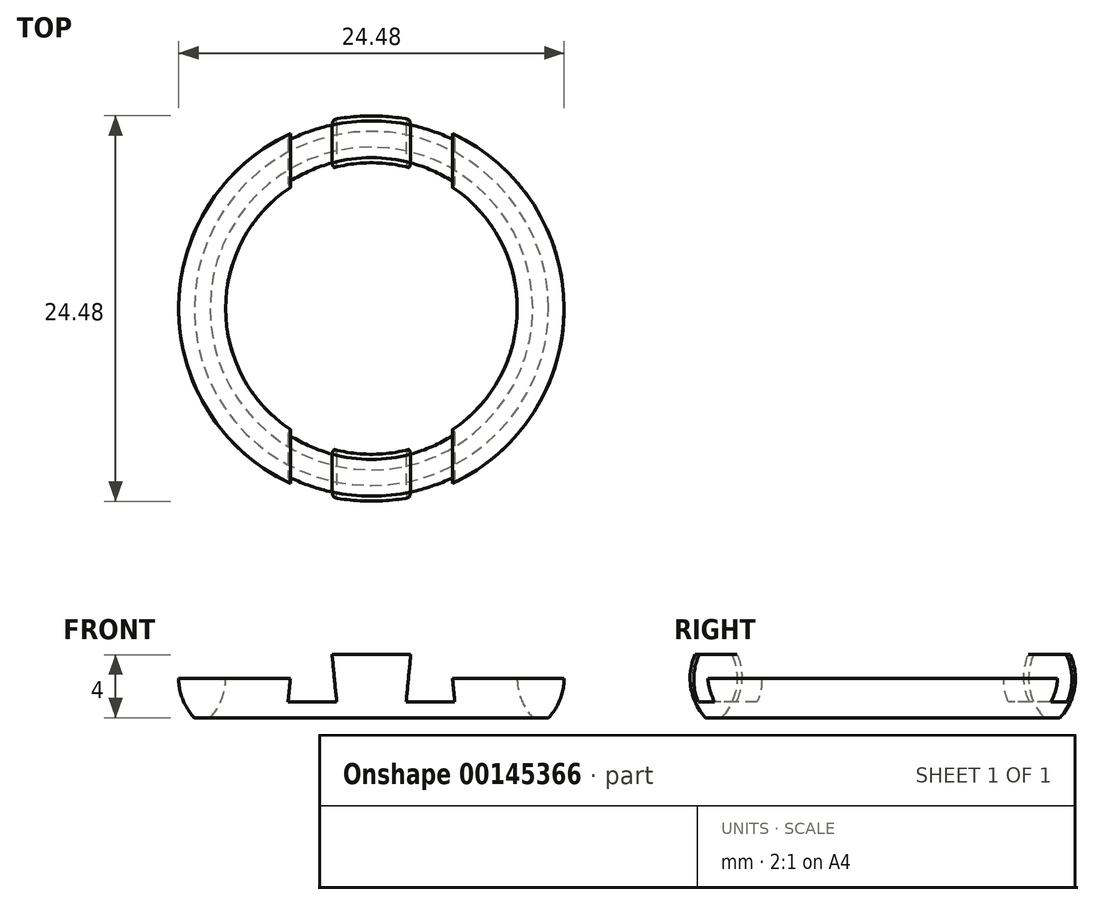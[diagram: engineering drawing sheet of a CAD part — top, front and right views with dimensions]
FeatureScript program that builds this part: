
annotation { "Feature Type Name" : "Feature", "Feature Type Description" : "" }
export const myFeature = defineFeature(function(context is Context, id is Id, definition is map)
    precondition{}
    {
        {
            var Q0;
            Q0=qCreatedBy(makeId("Front.planeOp"),FACE);
            var sketch = newSketch(context, id + "F0", { "sketchPlane" : qUnion([Q0])});
            skLineSegment(sketch, "E0", {"start": v(0, 0) * mm, "end": v(0, 5) * mm});
            skArc(sketch, "E1", {"start": v(-10.25, 0) * mm, "mid": v(-9.26, 2.5) * mm, "end": v(-10.25, 5) * mm});
            skLineSegment(sketch, "E2", {"start": v(-11.25, 5) * mm, "end": v(-10.25, 5) * mm});
            skLineSegment(sketch, "E3", {"start": v(-11.25, 0) * mm, "end": v(-10.25, 0) * mm});
            skArc(sketch, "E4", {"start": v(-11.25, 5) * mm, "mid": v(-12.24, 2.5) * mm, "end": v(-11.25, 0) * mm});
            skPoint(sketch, "E5.orphan", {"position": v(-12.25, 5) * mm});
            skPoint(sketch, "E6.orphan", {"position": v(-12.25, 0) * mm});
            skSolve(sketch);
        }
        {
            var Q0;
            Q0=qSketchRegion(id+"F0",true);
            var Q1;
            Q1=sQuery(id+"F0.wireOp",EDGE,"E0");
            revolve(context, id + "F1", {"entities" : qUnion([Q0]), "axis" : qUnion([Q1]), "revolveType" : RevolveType.FULL});
        }
        {
            var Q0;
            Q0=qCreatedBy(makeId("Front.planeOp"),FACE);
            var sketch = newSketch(context, id + "F2", { "sketchPlane" : qUnion([Q0])});
            skLineSegment(sketch, "E7", {"start": v(-12.26, 2.5) * mm, "end": v(-5.15, 2.5) * mm});
            skLineSegment(sketch, "E8", {"start": v(-12.26, 2.5) * mm, "end": v(-12.26, 5.63) * mm});
            skLineSegment(sketch, "E9", {"start": v(0, 0) * mm, "end": v(0, 4.5) * mm});
            skLineSegment(sketch, "E10", {"start": v(0, 2.5) * mm, "end": v(0, 3.83) * mm});
            skLineSegment(sketch, "E11", {"start": v(0, 2.5) * mm, "end": v(0, 3.47) * mm});
            skLineSegment(sketch, "E12", {"start": v(0, 2.5) * mm, "end": v(0, 4.5) * mm});
            skLineSegment(sketch, "E13", {"start": v(-2.5, 4) * mm, "end": v(-2.2, 1) * mm});
            skLineSegment(sketch, "E14.0", {"start": v(-5.3, 1) * mm, "end": v(-2.2, 1) * mm});
            skLineSegment(sketch, "E15.0.MirrorCS", {"start": v(-5.15, 2.5) * mm, "end": v(-5.3, 1) * mm});
            skLineSegment(sketch, "E16.trimOffspring", {"start": v(-2.5, 4) * mm, "end": v(0, 4) * mm});
            skLineSegment(sketch, "E17.0.MirrorCS", {"start": v(12.26, 2.5) * mm, "end": v(12.26, 5.63) * mm});
            skLineSegment(sketch, "E18.0.MirrorCS", {"start": v(12.26, 2.5) * mm, "end": v(5.15, 2.5) * mm});
            skLineSegment(sketch, "E19.0.MirrorCS", {"start": v(5.15, 2.5) * mm, "end": v(5.3, 1) * mm});
            skLineSegment(sketch, "E20.0.MirrorCS", {"start": v(5.3, 1) * mm, "end": v(2.2, 1) * mm});
            skLineSegment(sketch, "E21.0.MirrorCS", {"start": v(2.5, 4) * mm, "end": v(2.2, 1) * mm});
            skLineSegment(sketch, "E22.0.MirrorCS", {"start": v(2.5, 4) * mm, "end": v(0, 4) * mm});
            skLineSegment(sketch, "E23", {"start": v(-12.26, 5.63) * mm, "end": v(12.26, 5.63) * mm});
            skLineSegment(sketch, "E24.trimOffspring", {"start": v(0, 5.63) * mm, "end": v(0, 5.9) * mm});
            skPoint(sketch, "E25.0.MirrorCS.end.orphan", {"position": v(6.1, 2.5) * mm});
            skPoint(sketch, "E26.0.MirrorCS.start.orphan", {"position": v(6.25, 4) * mm});
            skPoint(sketch, "E27.orphan", {"position": v(5, 4) * mm});
            skPoint(sketch, "E28.0.MirrorCS.end.orphan", {"position": v(-6.1, 2.5) * mm});
            skPoint(sketch, "E28.0.MirrorCS.start.orphan", {"position": v(-6.25, 4) * mm});
            skPoint(sketch, "E29.orphan", {"position": v(-5, 4) * mm});
            skSolve(sketch);
        }
        {
            var Q0;
            Q0=makeQuery(id+"F2.imprint","IMPRINT",FACE,{"disambiguationData":[TD([[makeQuery(id+"F2.imprint","IMPRINT",EDGE,{"derivedFrom":sQuery(id+"F2.wireOp",EDGE,"E7")}),1.0]])]});
            extrude(context, id + "F3", {"entities" : qUnion([Q0]), "operationType" : NewBodyOperationType.REMOVE, "endBound" : BoundingType.SYMMETRIC, "oppositeDirection" : true, "depth" : 25 * mm});
        }
    });
